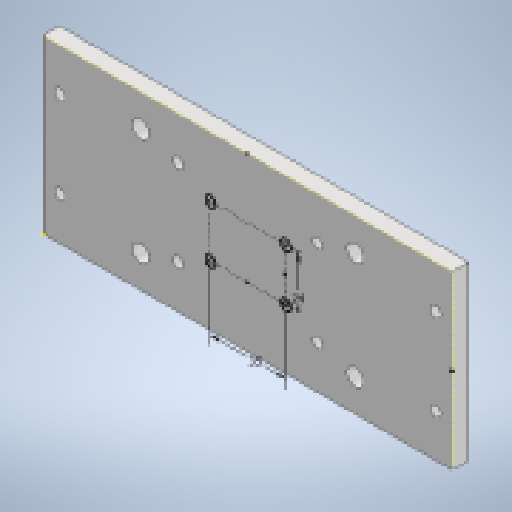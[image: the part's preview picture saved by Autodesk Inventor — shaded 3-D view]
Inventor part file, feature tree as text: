
AUTODESK INVENTOR PART (.ipt)
format: ipt  version: 2023 (Build 270158000, 158)  size: 168,448 bytes
history: native  units: mm
features: extrude x4, sketch x4
ambient origin geometry x8: Origin, YZ Plane, XZ Plane, XY Plane, X Axis, Y Axis, Z Axis, Center Point
bodies: Solid1 (feature_tree)
feature tree (8):
  extrude  "Extrusion1"  Depth=190.5mm
  extrude  "Extrusion2"  Depth=7.62mm
  extrude  "Extrusion3"  Depth=8.0mm
  extrude  "Extrusion4"  Depth=10.0mm
  sketch  "Sketch1"  dims[d0=80.0mm d1=190.5mm]
  sketch  "Sketch2"  dims[d2=7.62mm d3=0.0mm d4=100.0mm]
  sketch  "Sketch3"  dims[d5=50.0mm d6=8.0mm]
  sketch  "Sketch4"  dims[d7=7.62mm d8=0.0mm d9=5.0mm d10=55.0mm d11=40.0mm d12=60.0mm d13=10.0mm d14=0.0mm d15=5.0mm d16=35.0mm d17=24.0mm d18=14.0mm d19=10.0mm d20=0.0mm]
